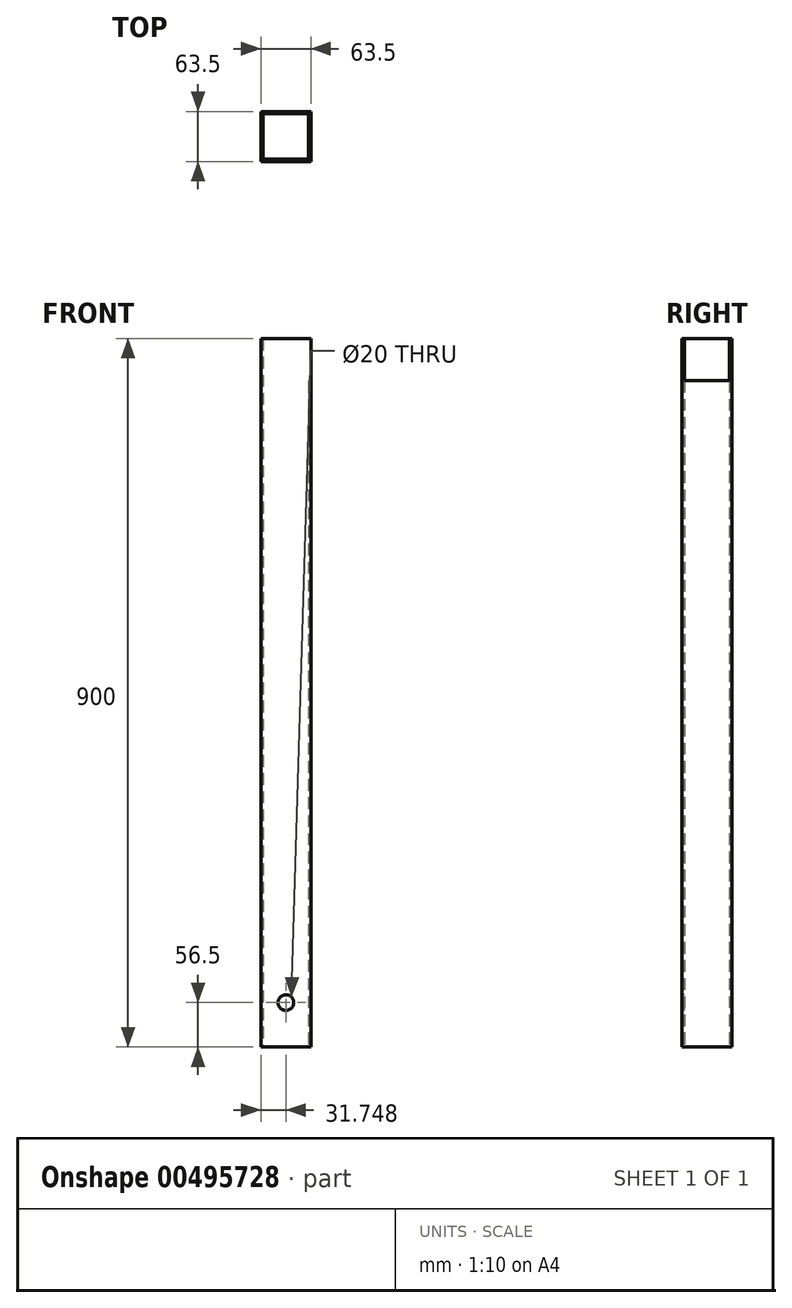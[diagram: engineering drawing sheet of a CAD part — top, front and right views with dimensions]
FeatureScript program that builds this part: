
annotation { "Feature Type Name" : "Feature", "Feature Type Description" : "" }
export const myFeature = defineFeature(function(context is Context, id is Id, definition is map)
    precondition{}
    {
        {
            var Q0;
            Q0=qCreatedBy(makeId("Top.planeOp"),FACE);
            var sketch = newSketch(context, id + "F0", { "sketchPlane" : qUnion([Q0])});
            skLineSegment(sketch, "E0.bottom", {"start": v(-27.53, 27.67) * mm, "end": v(29.97, 27.67) * mm});
            skLineSegment(sketch, "E0.top", {"start": v(-27.53, -29.83) * mm, "end": v(29.97, -29.83) * mm});
            skLineSegment(sketch, "E0.left", {"start": v(-27.53, 27.67) * mm, "end": v(-27.53, -29.83) * mm});
            skLineSegment(sketch, "E0.right", {"start": v(29.97, 27.67) * mm, "end": v(29.97, -29.83) * mm});
            skLineSegment(sketch, "E1.bottom", {"start": v(-30.53, 30.67) * mm, "end": v(32.97, 30.67) * mm});
            skLineSegment(sketch, "E1.top", {"start": v(-30.53, -32.83) * mm, "end": v(32.97, -32.83) * mm});
            skLineSegment(sketch, "E1.left", {"start": v(-30.53, 30.67) * mm, "end": v(-30.53, -32.83) * mm});
            skLineSegment(sketch, "E1.right", {"start": v(32.97, 30.67) * mm, "end": v(32.97, -32.83) * mm});
            skSolve(sketch);
        }
        {
            var Q0;
            Q0 = qSketchRegion(id + "F0", true);
            extrude(context, id + "F1", {"entities" : qUnion([Q0]), "depth" : 900 * mm});
        }
        {
            var Q0;
            Q0=makeQuery(id+"F1.opExtrude","SWEPT_FACE",FACE,{"disambiguationData":[OSD([sQuery(id+"F0.wireOp",EDGE,"E1.right")])]});
            var sketch = newSketch(context, id + "F2", { "sketchPlane" : qUnion([Q0])});
            skLineSegment(sketch, "E2.bottom", {"start": v(-29.83, 900) * mm, "end": v(27.67, 900) * mm});
            skLineSegment(sketch, "E2.top", {"start": v(-29.83, 846.5) * mm, "end": v(27.67, 846.5) * mm});
            skLineSegment(sketch, "E2.left", {"start": v(-29.83, 900) * mm, "end": v(-29.83, 846.5) * mm});
            skLineSegment(sketch, "E2.right", {"start": v(27.67, 900) * mm, "end": v(27.67, 846.5) * mm});
            skSolve(sketch);
        }
        {
            var Q0;
            Q0 = qSketchRegion(id + "F2", true);
            extrude(context, id + "F3", {"entities" : qUnion([Q0]), "operationType" : NewBodyOperationType.REMOVE, "oppositeDirection" : true, "depth" : 3 * mm});
        }
        {
            var Q0;
            Q0=makeQuery(id+"F1.opExtrude","SWEPT_FACE",FACE,{"disambiguationData":[OSD([sQuery(id+"F0.wireOp",EDGE,"E1.top")])]});
            var sketch = newSketch(context, id + "F4", { "sketchPlane" : qUnion([Q0])});
            skCircle(sketch, "E3", {"center": v(1.22, 56.5) * mm, "radius": 10 * mm});
            skSolve(sketch);
        }
        {
            var Q0;
            Q0 = qSketchRegion(id + "F4", true);
            extrude(context, id + "F5", {"entities" : qUnion([Q0]), "operationType" : NewBodyOperationType.REMOVE, "oppositeDirection" : true, "depth" : 3 * mm, "offsetDistance" : 25 * mm});
        }
    });
